# Revit family: Nivellierbare Kassette für Revisionsöffnung, RKNUZD3, 20-25, 4
name_source: partatom
category: Generic Models
revit_build: Autodesk Revit 2015 (Build: 20140606_1530(x64)
units: mm (PartAtom-declared; Revit-internal decimal feet)

## types (4) — shared parameters
Height 1 = 29 mm  [stored 0.0951444 ft]
Length = 199 mm  [stored 0.652887 ft]
Manufacturer = OBO Bettermann
URL = http://www.obo-bettermann.com
Width = 199 mm  [stored 0.652887 ft]

## per-type parameters (varying)
| type | Cut depth | GTIN | Height | Manufacturer Art.No. | Material |
| RKN2 UZD3 4VS20 | 20 mm  [stored 0.0656168 ft] | 4012195867883 | 90 mm  [stored 0.295276 ft] | 7409058 | Stainless Steel, Polished |
| RKN2 UZD3 4MS20 | 20 mm  [stored 0.0656168 ft] | 4012195867838 | 90 mm  [stored 0.295276 ft] | 7409052 | Brass, Soft Yellow, Welded |
| RKN2 UZD3 4VS25 | 25 mm  [stored 0.082021 ft] | 4012195867906 | 95 mm | 7409060 | Stainless Steel |
| RKN2 UZD3 4MS25 | 25 mm  [stored 0.082021 ft] | 4012195867845 | 95 mm | 7409054 | Brass, Soft Yellow, Welded |

note: column(s) folded — value = type name in every type: Article Type

note: [stored X ft] marks values corroborated as IEEE doubles in the binary element streams (Revit-internal decimal feet)

## geometry (parser evidence)
native form markers: Sweep x2
no freeform markers — native parametric forms only
